# Revit family: Haworth_Typical_Parametric_ResideBeside_L_HighStorage
name_source: partatom
category: Furniture Systems
revit_build: Autodesk Revit Architecture 2014 (Build: 20130308_1515(x64)
units: mm (PartAtom-declared; Revit-internal decimal feet)

## types (2) — shared parameters
Actual Storage Depth = 18"
Angled Double Leg = No
Assembly Code = E2020200
Blade Pull = Yes
Blotter = Yes
Blotter Finish = Haworth - Trim - Polymer Colors - Snow TR-FM
Blotter Offset = 15"
Description = Haworth_Typical_Parametric_ResideBeside_L_HighStorage
File Cabinet Finish = Haworth - Laminate - Columbian Walnut H-0KG
File Drawer Finish = Haworth - Metal - Brushed Aluminum
File Pull Finish = Haworth - Metal - Polished Aluminum
Hardware Finish = Haworth - Metal - Polished Aluminum
Hoop Leg = Yes
J Pull = No
Manufacturer = Haworth
Max Height = 74"
Max Storage Length = 72"
Max Worksurface Depth = 30"
Max Worksurface Length = 96"
Maximum Length Storage = 72 in.
Maximum Length Worksurface = 96 in.
Min Storage Length = 48"
Min Worksurface Depth = 24"
Min Worksurface Length = 60"
Minimum Length Storage = 48 in.
Minimum Length Worksurface = 60 in.
Model = Haworth_Typical_Parametric_ResideBeside_L_HighStorage
Offset Screen Center = 1/4"
Revision = 1
Screen = Yes
Screen Finish = Haworth - Fabric - Tellure - Steel 3A-39
Screen Offset = 1/2"
Seat Arm Cap Finish = Haworth - Paint - Smoke
Seat Back Upholstery Finish = Haworth - Fabric - Zody Mesh - Comfort MA-002
Seat Cushion Finish = Haworth - Fabric - Zinger - Gravel NI-4
Seat Shell Finish = Haworth - Metal - Polished Aluminum
Seat Support Finish = Haworth - Paint - Smoke
Size = Verify Final Dim. w/ Haworth
Stanchion = Yes
Stanchion Shelf Finish = Haworth - Laminate - Columbian Walnut H-0KG
Stanchion Support Finish = Haworth - Paint - Smoke
Storage Middle = 9"
Straight Double Leg = No
Support Offset = 6 1/2"
Sustainability Info = www.haworth.com/en-us/About-Us/Sustainability/Pages/Vision.aspx
Task Chair = Yes
URL = http://haworth.com
URL - Product = http://haworth.com
Warranty = http://haworth.com
Worksurface Edge Finish = Haworth - Laminate - Columbian Walnut H-0KG
Worksurface Finish = Haworth - Laminate - Columbian Walnut H-0KG

## per-type parameters (varying)
| type | Actual Storage Length | Actual Worksurface Depth | Actual Worksurface Length | Chair Location | Half Worksurface Depth | Screen Length | Storage Length | Worksurface Depth | Worksurface Length |
| 8x7 | 54" | 30" | 96" | 39" | 15" | 66" | 54" | 30" | 96" |
| 5x6 | 48" | 24" | 60" | 21" | 12" | 30" | 48" | 24" | 60" |

## geometry (parser evidence)
native form markers: Blend x63, Sweep x49
no freeform markers — native parametric forms only
